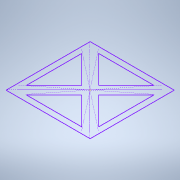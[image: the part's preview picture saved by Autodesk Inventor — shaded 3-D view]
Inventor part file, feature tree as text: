
AUTODESK INVENTOR PART (.ipt)
format: ipt  version: 2022 (Build 260153000, 153)  size: 92,672 bytes
history: native  units: mm
features: sketch x1
ambient origin geometry x8: Origin, YZ Plane, XZ Plane, XY Plane, X Axis, Y Axis, Z Axis, Center Point
feature tree (1):
  sketch  "Sketch2"
